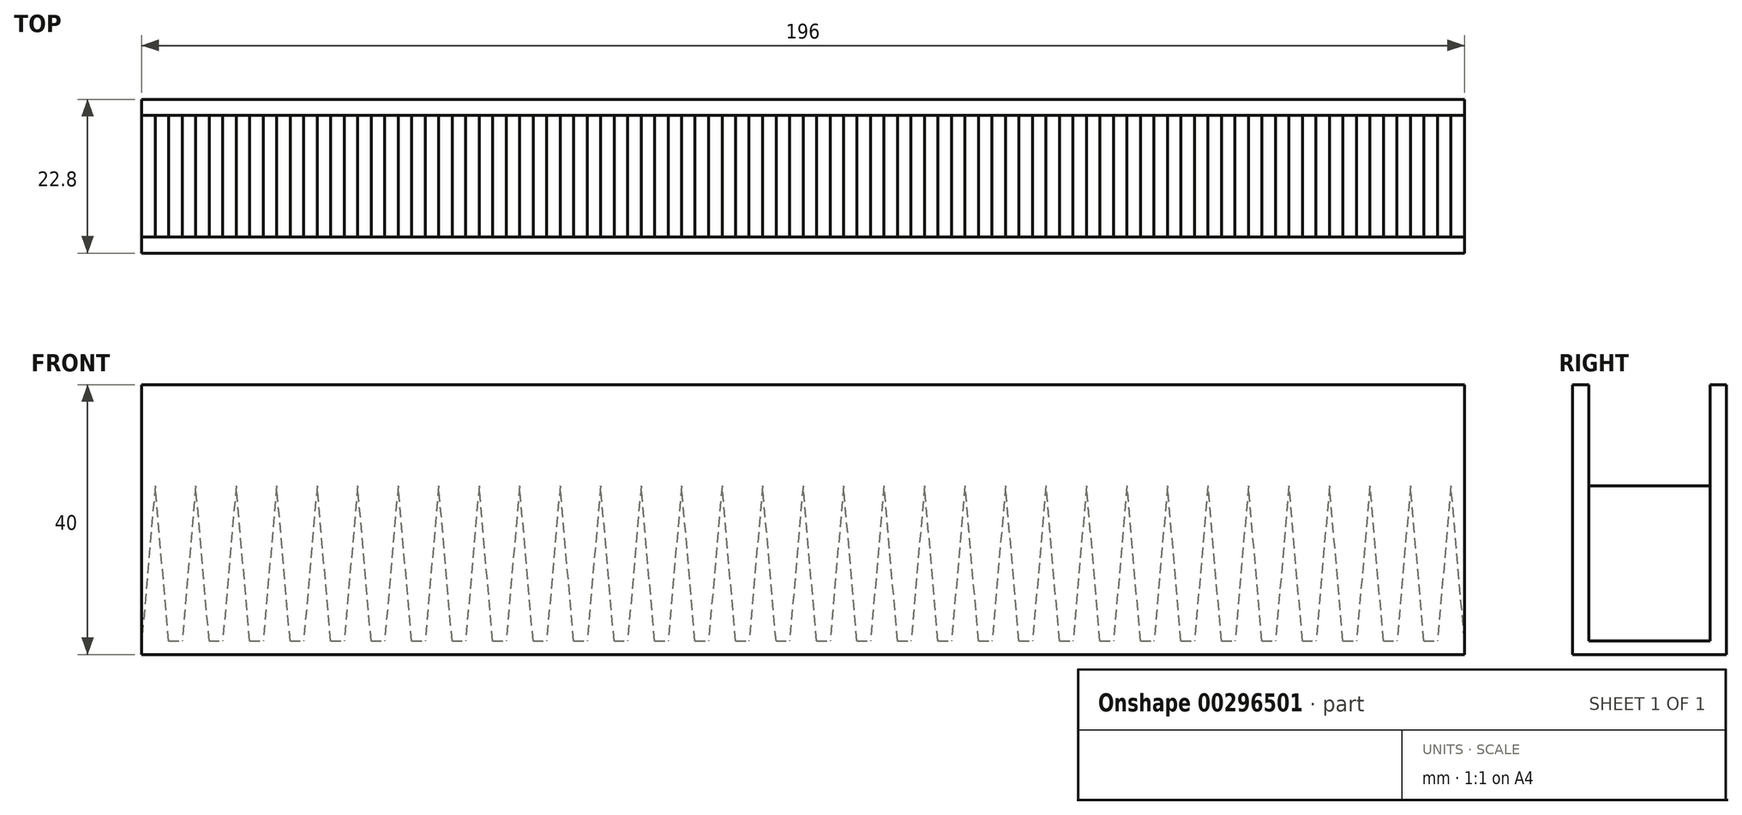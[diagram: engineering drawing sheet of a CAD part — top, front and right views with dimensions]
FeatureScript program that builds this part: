
annotation { "Feature Type Name" : "Feature", "Feature Type Description" : "" }
export const myFeature = defineFeature(function(context is Context, id is Id, definition is map)
    precondition{}
    {
        {
            var Q0;
            Q0=qCreatedBy(makeId("Top.planeOp"),FACE);
            var sketch = newSketch(context, id + "F0", { "sketchPlane" : qUnion([Q0])});
            skLineSegment(sketch, "E0.bottom", {"start": v(0, 0) * mm, "end": v(200, 0) * mm});
            skLineSegment(sketch, "E0.top", {"start": v(0, 18) * mm, "end": v(200, 18) * mm});
            skLineSegment(sketch, "E0.left", {"start": v(0, 0) * mm, "end": v(0, 18) * mm});
            skLineSegment(sketch, "E0.right", {"start": v(200, 0) * mm, "end": v(200, 18) * mm});
            skSolve(sketch);
        }
        {
            var Q0;
            Q0 = qSketchRegion(id + "F0", true);
            extrude(context, id + "F1", {"entities" : qUnion([Q0]), "depth" : 2 * mm});
        }
        {
            var Q0;
            Q0=makeQuery(id+"F1.opExtrude","CAP_FACE",FACE,{"disambiguationData":[OSD([sQuery(id+"F0.wireOp",EDGE,"E0.bottom"),sQuery(id+"F0.wireOp",EDGE,"E0.top"),sQuery(id+"F0.wireOp",EDGE,"E0.left"),sQuery(id+"F0.wireOp",EDGE,"E0.right")])],"isStart":true});
            var sketch = newSketch(context, id + "F2", { "sketchPlane" : qUnion([Q0])});
            skLineSegment(sketch, "E1.bottom", {"start": v(0, 0) * mm, "end": v(200, 0) * mm});
            skLineSegment(sketch, "E1.top", {"start": v(0, 2.4) * mm, "end": v(200, 2.4) * mm});
            skLineSegment(sketch, "E1.left", {"start": v(0, 0) * mm, "end": v(0, 2.4) * mm});
            skLineSegment(sketch, "E1.right", {"start": v(200, 0) * mm, "end": v(200, 2.4) * mm});
            skLineSegment(sketch, "E2.bottom", {"start": v(0, -18) * mm, "end": v(200, -18) * mm});
            skLineSegment(sketch, "E2.top", {"start": v(0, -20.4) * mm, "end": v(200, -20.4) * mm});
            skLineSegment(sketch, "E2.left", {"start": v(0, -18) * mm, "end": v(0, -20.4) * mm});
            skLineSegment(sketch, "E2.right", {"start": v(200, -18) * mm, "end": v(200, -20.4) * mm});
            skSolve(sketch);
        }
        {
            var Q0;
            Q0 = qSketchRegion(id + "F2", true);
            extrude(context, id + "F3", {"entities" : qUnion([Q0]), "operationType" : NewBodyOperationType.ADD, "oppositeDirection" : true, "depth" : 40 * mm});
        }
        {
            var Q0;
            Q0=makeQuery(id+"F3.opExtrude","SWEPT_FACE",FACE,{"disambiguationData":[OSD([sQuery(id+"F2.wireOp",EDGE,"E2.bottom")])]});
            var sketch = newSketch(context, id + "F4", { "sketchPlane" : qUnion([Q0])});
            skLineSegment(sketch, "E3", {"start": v(0, 2) * mm, "end": v(2, 25) * mm});
            skLineSegment(sketch, "E4", {"start": v(2, 25) * mm, "end": v(4, 2) * mm});
            skLineSegment(sketch, "E5", {"start": v(4, 2) * mm, "end": v(0, 2) * mm});
            skLineSegment(sketch, "E6.1.0.0", {"start": v(8, 25) * mm, "end": v(10, 2) * mm});
            skLineSegment(sketch, "E6.1.0.1", {"start": v(10, 2) * mm, "end": v(6, 2) * mm});
            skLineSegment(sketch, "E6.1.0.2", {"start": v(6, 2) * mm, "end": v(8, 25) * mm});
            skLineSegment(sketch, "E6.2.0.0", {"start": v(14, 25) * mm, "end": v(16, 2) * mm});
            skLineSegment(sketch, "E6.2.0.1", {"start": v(16, 2) * mm, "end": v(12, 2) * mm});
            skLineSegment(sketch, "E6.2.0.2", {"start": v(12, 2) * mm, "end": v(14, 25) * mm});
            skLineSegment(sketch, "E6.3.0.0", {"start": v(20, 25) * mm, "end": v(22, 2) * mm});
            skLineSegment(sketch, "E6.3.0.1", {"start": v(22, 2) * mm, "end": v(18, 2) * mm});
            skLineSegment(sketch, "E6.3.0.2", {"start": v(18, 2) * mm, "end": v(20, 25) * mm});
            skLineSegment(sketch, "E6.4.0.0", {"start": v(26, 25) * mm, "end": v(28, 2) * mm});
            skLineSegment(sketch, "E6.4.0.1", {"start": v(28, 2) * mm, "end": v(24, 2) * mm});
            skLineSegment(sketch, "E6.4.0.2", {"start": v(24, 2) * mm, "end": v(26, 25) * mm});
            skLineSegment(sketch, "E6.5.0.0", {"start": v(32, 25) * mm, "end": v(34, 2) * mm});
            skLineSegment(sketch, "E6.5.0.1", {"start": v(34, 2) * mm, "end": v(30, 2) * mm});
            skLineSegment(sketch, "E6.5.0.2", {"start": v(30, 2) * mm, "end": v(32, 25) * mm});
            skLineSegment(sketch, "E6.6.0.0", {"start": v(38, 25) * mm, "end": v(40, 2) * mm});
            skLineSegment(sketch, "E6.6.0.1", {"start": v(40, 2) * mm, "end": v(36, 2) * mm});
            skLineSegment(sketch, "E6.6.0.2", {"start": v(36, 2) * mm, "end": v(38, 25) * mm});
            skLineSegment(sketch, "E6.7.0.0", {"start": v(44, 25) * mm, "end": v(46, 2) * mm});
            skLineSegment(sketch, "E6.7.0.1", {"start": v(46, 2) * mm, "end": v(42, 2) * mm});
            skLineSegment(sketch, "E6.7.0.2", {"start": v(42, 2) * mm, "end": v(44, 25) * mm});
            skLineSegment(sketch, "E6.8.0.0", {"start": v(50, 25) * mm, "end": v(52, 2) * mm});
            skLineSegment(sketch, "E6.8.0.1", {"start": v(52, 2) * mm, "end": v(48, 2) * mm});
            skLineSegment(sketch, "E6.8.0.2", {"start": v(48, 2) * mm, "end": v(50, 25) * mm});
            skLineSegment(sketch, "E6.9.0.0", {"start": v(56, 25) * mm, "end": v(58, 2) * mm});
            skLineSegment(sketch, "E6.9.0.1", {"start": v(58, 2) * mm, "end": v(54, 2) * mm});
            skLineSegment(sketch, "E6.9.0.2", {"start": v(54, 2) * mm, "end": v(56, 25) * mm});
            skLineSegment(sketch, "E6.10.0.0", {"start": v(62, 25) * mm, "end": v(64, 2) * mm});
            skLineSegment(sketch, "E6.10.0.1", {"start": v(64, 2) * mm, "end": v(60, 2) * mm});
            skLineSegment(sketch, "E6.10.0.2", {"start": v(60, 2) * mm, "end": v(62, 25) * mm});
            skLineSegment(sketch, "E6.11.0.0", {"start": v(68, 25) * mm, "end": v(70, 2) * mm});
            skLineSegment(sketch, "E6.11.0.1", {"start": v(70, 2) * mm, "end": v(66, 2) * mm});
            skLineSegment(sketch, "E6.11.0.2", {"start": v(66, 2) * mm, "end": v(68, 25) * mm});
            skLineSegment(sketch, "E6.12.0.0", {"start": v(74, 25) * mm, "end": v(76, 2) * mm});
            skLineSegment(sketch, "E6.12.0.1", {"start": v(76, 2) * mm, "end": v(72, 2) * mm});
            skLineSegment(sketch, "E6.12.0.2", {"start": v(72, 2) * mm, "end": v(74, 25) * mm});
            skLineSegment(sketch, "E6.13.0.0", {"start": v(80, 25) * mm, "end": v(82, 2) * mm});
            skLineSegment(sketch, "E6.13.0.1", {"start": v(82, 2) * mm, "end": v(78, 2) * mm});
            skLineSegment(sketch, "E6.13.0.2", {"start": v(78, 2) * mm, "end": v(80, 25) * mm});
            skLineSegment(sketch, "E6.14.0.0", {"start": v(86, 25) * mm, "end": v(88, 2) * mm});
            skLineSegment(sketch, "E6.14.0.1", {"start": v(88, 2) * mm, "end": v(84, 2) * mm});
            skLineSegment(sketch, "E6.14.0.2", {"start": v(84, 2) * mm, "end": v(86, 25) * mm});
            skLineSegment(sketch, "E6.15.0.0", {"start": v(92, 25) * mm, "end": v(94, 2) * mm});
            skLineSegment(sketch, "E6.15.0.1", {"start": v(94, 2) * mm, "end": v(90, 2) * mm});
            skLineSegment(sketch, "E6.15.0.2", {"start": v(90, 2) * mm, "end": v(92, 25) * mm});
            skLineSegment(sketch, "E6.16.0.0", {"start": v(98, 25) * mm, "end": v(100, 2) * mm});
            skLineSegment(sketch, "E6.16.0.1", {"start": v(100, 2) * mm, "end": v(96, 2) * mm});
            skLineSegment(sketch, "E6.16.0.2", {"start": v(96, 2) * mm, "end": v(98, 25) * mm});
            skLineSegment(sketch, "E6.17.0.0", {"start": v(104, 25) * mm, "end": v(106, 2) * mm});
            skLineSegment(sketch, "E6.17.0.1", {"start": v(106, 2) * mm, "end": v(102, 2) * mm});
            skLineSegment(sketch, "E6.17.0.2", {"start": v(102, 2) * mm, "end": v(104, 25) * mm});
            skLineSegment(sketch, "E6.18.0.0", {"start": v(110, 25) * mm, "end": v(112, 2) * mm});
            skLineSegment(sketch, "E6.18.0.1", {"start": v(112, 2) * mm, "end": v(108, 2) * mm});
            skLineSegment(sketch, "E6.18.0.2", {"start": v(108, 2) * mm, "end": v(110, 25) * mm});
            skLineSegment(sketch, "E6.19.0.0", {"start": v(116, 25) * mm, "end": v(118, 2) * mm});
            skLineSegment(sketch, "E6.19.0.1", {"start": v(118, 2) * mm, "end": v(114, 2) * mm});
            skLineSegment(sketch, "E6.19.0.2", {"start": v(114, 2) * mm, "end": v(116, 25) * mm});
            skLineSegment(sketch, "E6.20.0.0", {"start": v(122, 25) * mm, "end": v(124, 2) * mm});
            skLineSegment(sketch, "E6.20.0.1", {"start": v(124, 2) * mm, "end": v(120, 2) * mm});
            skLineSegment(sketch, "E6.20.0.2", {"start": v(120, 2) * mm, "end": v(122, 25) * mm});
            skLineSegment(sketch, "E6.21.0.0", {"start": v(128, 25) * mm, "end": v(130, 2) * mm});
            skLineSegment(sketch, "E6.21.0.1", {"start": v(130, 2) * mm, "end": v(126, 2) * mm});
            skLineSegment(sketch, "E6.21.0.2", {"start": v(126, 2) * mm, "end": v(128, 25) * mm});
            skLineSegment(sketch, "E6.22.0.0", {"start": v(134, 25) * mm, "end": v(136, 2) * mm});
            skLineSegment(sketch, "E6.22.0.1", {"start": v(136, 2) * mm, "end": v(132, 2) * mm});
            skLineSegment(sketch, "E6.22.0.2", {"start": v(132, 2) * mm, "end": v(134, 25) * mm});
            skLineSegment(sketch, "E6.23.0.0", {"start": v(140, 25) * mm, "end": v(142, 2) * mm});
            skLineSegment(sketch, "E6.23.0.1", {"start": v(142, 2) * mm, "end": v(138, 2) * mm});
            skLineSegment(sketch, "E6.23.0.2", {"start": v(138, 2) * mm, "end": v(140, 25) * mm});
            skLineSegment(sketch, "E6.24.0.0", {"start": v(146, 25) * mm, "end": v(148, 2) * mm});
            skLineSegment(sketch, "E6.24.0.1", {"start": v(148, 2) * mm, "end": v(144, 2) * mm});
            skLineSegment(sketch, "E6.24.0.2", {"start": v(144, 2) * mm, "end": v(146, 25) * mm});
            skLineSegment(sketch, "E6.25.0.0", {"start": v(152, 25) * mm, "end": v(154, 2) * mm});
            skLineSegment(sketch, "E6.25.0.1", {"start": v(154, 2) * mm, "end": v(150, 2) * mm});
            skLineSegment(sketch, "E6.25.0.2", {"start": v(150, 2) * mm, "end": v(152, 25) * mm});
            skLineSegment(sketch, "E6.26.0.0", {"start": v(158, 25) * mm, "end": v(160, 2) * mm});
            skLineSegment(sketch, "E6.26.0.1", {"start": v(160, 2) * mm, "end": v(156, 2) * mm});
            skLineSegment(sketch, "E6.26.0.2", {"start": v(156, 2) * mm, "end": v(158, 25) * mm});
            skLineSegment(sketch, "E6.27.0.0", {"start": v(164, 25) * mm, "end": v(166, 2) * mm});
            skLineSegment(sketch, "E6.27.0.1", {"start": v(166, 2) * mm, "end": v(162, 2) * mm});
            skLineSegment(sketch, "E6.27.0.2", {"start": v(162, 2) * mm, "end": v(164, 25) * mm});
            skLineSegment(sketch, "E6.28.0.0", {"start": v(170, 25) * mm, "end": v(172, 2) * mm});
            skLineSegment(sketch, "E6.28.0.1", {"start": v(172, 2) * mm, "end": v(168, 2) * mm});
            skLineSegment(sketch, "E6.28.0.2", {"start": v(168, 2) * mm, "end": v(170, 25) * mm});
            skLineSegment(sketch, "E6.29.0.0", {"start": v(176, 25) * mm, "end": v(178, 2) * mm});
            skLineSegment(sketch, "E6.29.0.1", {"start": v(178, 2) * mm, "end": v(174, 2) * mm});
            skLineSegment(sketch, "E6.29.0.2", {"start": v(174, 2) * mm, "end": v(176, 25) * mm});
            skLineSegment(sketch, "E6.30.0.0", {"start": v(182, 25) * mm, "end": v(184, 2) * mm});
            skLineSegment(sketch, "E6.30.0.1", {"start": v(184, 2) * mm, "end": v(180, 2) * mm});
            skLineSegment(sketch, "E6.30.0.2", {"start": v(180, 2) * mm, "end": v(182, 25) * mm});
            skLineSegment(sketch, "E6.31.0.0", {"start": v(188, 25) * mm, "end": v(190, 2) * mm});
            skLineSegment(sketch, "E6.31.0.1", {"start": v(190, 2) * mm, "end": v(186, 2) * mm});
            skLineSegment(sketch, "E6.31.0.2", {"start": v(186, 2) * mm, "end": v(188, 25) * mm});
            skLineSegment(sketch, "E6.32.0.0", {"start": v(194, 25) * mm, "end": v(196, 2) * mm});
            skLineSegment(sketch, "E6.32.0.1", {"start": v(196, 2) * mm, "end": v(192, 2) * mm});
            skLineSegment(sketch, "E6.32.0.2", {"start": v(192, 2) * mm, "end": v(194, 25) * mm});
            skLineSegment(sketch, "E6.direction1", {"start": v(0, 2) * mm, "end": v(6, 2) * mm, "construction": true});
            skSolve(sketch);
        }
        {
            var Q0;
            Q0 = qSketchRegion(id + "F4", true);
            var Q1;
            Q1=makeQuery(id+"F3.opExtrude","SWEPT_FACE",FACE,{"disambiguationData":[OSD([sQuery(id+"F2.wireOp",EDGE,"E1.bottom")])]});
            extrude(context, id + "F5", {"entities" : qUnion([Q0]), "operationType" : NewBodyOperationType.ADD, "endBound" : BoundingType.UP_TO_SURFACE, "endBoundEntityFace" : qUnion([Q1]), "depth" : 25 * mm});
        }
        {
            var Q0;
            Q0=makeQuery(id+"F3.opExtrude","SWEPT_FACE",FACE,{"disambiguationData":[OSD([sQuery(id+"F2.wireOp",EDGE,"E2.top")])]});
            var sketch = newSketch(context, id + "F6", { "sketchPlane" : qUnion([Q0])});
            skLineSegment(sketch, "E7.bottom", {"start": v(-200, 40) * mm, "end": v(-196, 40) * mm});
            skLineSegment(sketch, "E7.top", {"start": v(-200, 0) * mm, "end": v(-196, 0) * mm});
            skLineSegment(sketch, "E7.left", {"start": v(-200, 40) * mm, "end": v(-200, 0) * mm});
            skLineSegment(sketch, "E7.right", {"start": v(-196, 40) * mm, "end": v(-196, 0) * mm});
            skSolve(sketch);
        }
        {
            var Q0;
            Q0 = qSketchRegion(id + "F6", true);
            extrude(context, id + "F7", {"entities" : qUnion([Q0]), "operationType" : NewBodyOperationType.REMOVE, "endBound" : BoundingType.THROUGH_ALL, "oppositeDirection" : true, "depth" : 25 * mm});
        }
    });
